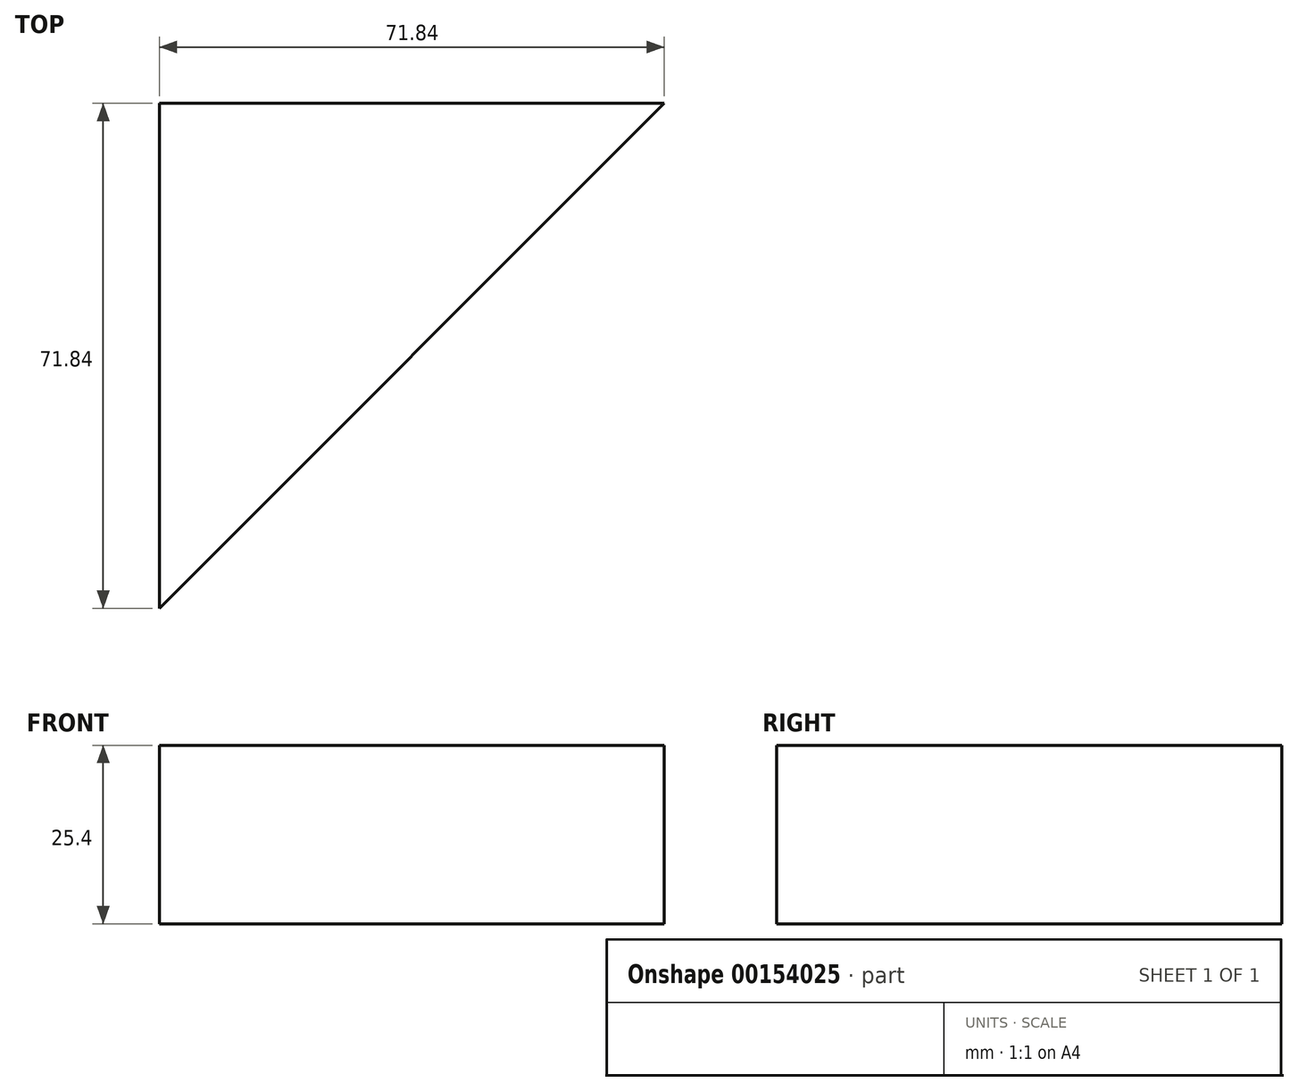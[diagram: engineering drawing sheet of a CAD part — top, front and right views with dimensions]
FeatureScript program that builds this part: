
annotation { "Feature Type Name" : "Feature", "Feature Type Description" : "" }
export const myFeature = defineFeature(function(context is Context, id is Id, definition is map)
    precondition{}
    {
        {
            var Q0;
            Q0=qCreatedBy(makeId("Top.planeOp"),FACE);
            var sketch = newSketch(context, id + "F0", { "sketchPlane" : qUnion([Q0])});
            skLineSegment(sketch, "E0", {"start": v(0, 0) * mm, "end": v(0, -71.84) * mm});
            skLineSegment(sketch, "E1", {"start": v(0, -71.84) * mm, "end": v(71.84, 0) * mm});
            skLineSegment(sketch, "E2", {"start": v(71.84, 0) * mm, "end": v(0, 0) * mm});
            skPoint(sketch, "E3", {"position": v(0, 0) * mm});
            skSolve(sketch);
        }
        {
            var Q0;
            Q0 = qSketchRegion(id + "F0", true);
            extrude(context, id + "F1", {"entities" : qUnion([Q0]), "depth" : 25.4 * mm});
        }
    });
